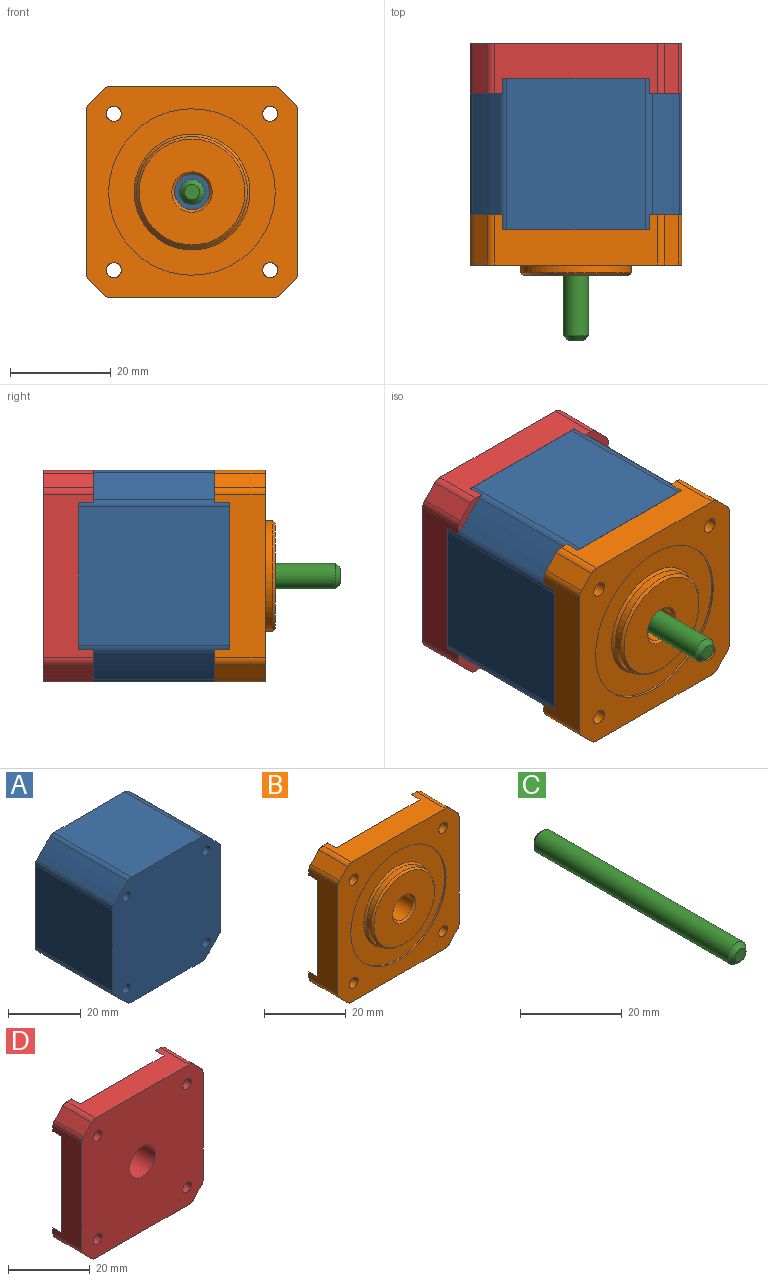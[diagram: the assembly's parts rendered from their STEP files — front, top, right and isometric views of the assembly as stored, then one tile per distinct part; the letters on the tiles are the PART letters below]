
ASSEMBLY  parts=4 mates=3
PART A: 22 faces, bbox 42x30x42 mm
  f0: cylinder r=55mm len=30mm, axis (0,1,0), area 230.4mm2, adj f8,f9,f10,f17
  f1: plane 30x27.54mm, normal (1,0,0), area 826.2mm2, adj f8,f9,f10,f11
  f2: cylinder r=55mm len=30mm, axis (0,1,0), area 230.4mm2, adj f8,f9,f11,f12
  f3: plane 30x27.54mm, normal (0,0,1), area 826.2mm2, adj f8,f9,f12,f13
  f4: cylinder r=55mm len=30mm, axis (0,1,0), area 230.4mm2, adj f8,f9,f13,f14
  f5: plane 30x27.54mm, normal (-1,0,0), area 826.2mm2, adj f8,f9,f14,f15
  f6: cylinder r=55mm len=30mm, axis (0,1,0), area 230.4mm2, adj f8,f9,f15,f16
  f7: plane 30x27.54mm, normal (0,0,-1), area 826.2mm2, adj f8,f9,f16,f17
  f8: plane 42x42mm, normal (0,-1,0), area 1655.7mm2, adj f0,f1,f2,f3,f4,f5,f6,f7
  f9: plane 42x42mm, normal (0,1,0), area 1655.7mm2, adj f0,f1,f2,f3,f4,f5,f6,f7
  f10: cylinder r=2mm len=30mm, axis (0,1,0), area 42.9mm2, adj f0,f1,f8,f9
  f11: cylinder r=2mm len=30mm, axis (0,1,0), area 42.9mm2, adj f1,f2,f8,f9
  f12: cylinder r=2mm len=30mm, axis (0,1,0), area 42.9mm2, adj f2,f3,f8,f9
  f13: cylinder r=2mm len=30mm, axis (0,1,0), area 42.9mm2, adj f3,f4,f8,f9
  f14: cylinder r=2mm len=30mm, axis (0,1,0), area 42.9mm2, adj f4,f5,f8,f9
  f15: cylinder r=2mm len=30mm, axis (0,1,0), area 42.9mm2, adj f5,f6,f8,f9
  f16: cylinder r=2mm len=30mm, axis (0,1,0), area 42.9mm2, adj f6,f7,f8,f9
  f17: cylinder r=2mm len=30mm, axis (0,1,0), area 42.9mm2, adj f0,f7,f8,f9
  f18: cylinder r=1.5mm len=30mm, axis (0,-1,0), area 282.7mm2, adj f8,f9
  f19: cylinder r=1.5mm len=30mm, axis (0,-1,0), area 282.7mm2, adj f8,f9
  f20: cylinder r=1.5mm len=30mm, axis (0,-1,0), area 282.7mm2, adj f8,f9
  f21: cylinder r=1.5mm len=30mm, axis (0,-1,0), area 282.7mm2, adj f8,f9
PART B: 38 faces, bbox 42x12x42 mm
  f0: plane 32.34x10mm, normal (1,0,0), area 236.4mm2, adj f3,f4,f9,f20,f21,f29,f31,f32
  f1: plane 32.34x10mm, normal (0,0,1), area 236.4mm2, adj f2,f3,f9,f18,f19,f29,f30,f31
  f2: plane 6.49x6.49mm, normal (0,1,0), area 11.7mm2, adj f1,f7,f13,f19,f23,f30
  f3: plane 6.49x6.49mm, normal (0,1,0), area 11.7mm2, adj f0,f1,f12,f18,f21,f31
  f4: plane 6.49x6.49mm, normal (0,1,0), area 11.7mm2, adj f0,f8,f11,f20,f25,f32
  f5: plane 6.49x6.49mm, normal (0,1,0), area 11.7mm2, adj f7,f8,f10,f22,f24,f33
  f6: cylinder r=3.5mm len=8.5mm, axis (0,-1,0), area 186.9mm2, adj f27,f29
  f7: plane 32.34x10mm, normal (-1,0,0), area 236.4mm2, adj f2,f5,f9,f22,f23,f29,f30,f33
  f8: plane 32.34x10mm, normal (0,0,-1), area 236.4mm2, adj f4,f5,f9,f24,f25,f29,f32,f33
  f9: plane 42x42mm, normal (0,-1,0), area 847.7mm2, adj f0,f1,f7,f8,f10,f11,f12,f13
  f10: plane 10x2.83mm, normal (-0.71,0,-0.71), area 40mm2, adj f5,f9,f22,f24
  f11: plane 10x2.83mm, normal (0.71,0,-0.71), area 40mm2, adj f4,f9,f20,f25
  f12: plane 10x2.83mm, normal (0.71,0,0.71), area 40mm2, adj f3,f9,f18,f21
  f13: plane 10x2.83mm, normal (-0.71,0,0.71), area 40mm2, adj f2,f9,f19,f23
  f14: cylinder r=16.5mm len=33mm, axis (0,-1,0), area 51.8mm2, adj f9,f15
  f15: plane 33x33mm, normal (0,-1,0), area 439.8mm2, adj f14,f26
  f16: cylinder r=11mm len=22mm, axis (0,1,0), area 103.7mm2, adj f26,f28
  f17: plane 21x21mm, normal (0,-1,0), area 296.1mm2, adj f27,f28
  f18: cylinder r=2mm len=10mm, axis (0,-1,0), area 15.7mm2, adj f1,f3,f9,f12
  f19: cylinder r=2mm len=10mm, axis (0,-1,0), area 15.7mm2, adj f1,f2,f9,f13
  f20: cylinder r=2mm len=10mm, axis (0,1,0), area 15.7mm2, adj f0,f4,f9,f11
  f21: cylinder r=2mm len=10mm, axis (0,1,0), area 15.7mm2, adj f0,f3,f9,f12
  f22: cylinder r=2mm len=10mm, axis (0,-1,0), area 15.7mm2, adj f5,f7,f9,f10
  f23: cylinder r=2mm len=10mm, axis (0,-1,0), area 15.7mm2, adj f2,f7,f9,f13
  f24: cylinder r=2mm len=10mm, axis (0,1,0), area 15.7mm2, adj f5,f8,f9,f10
  f25: cylinder r=2mm len=10mm, axis (0,1,0), area 15.7mm2, adj f4,f8,f9,f11
  f26: cone r=11mm half-angle=45deg, axis (0,1,0), area 50mm2, adj f15,f16
  f27: cone r=3.5mm half-angle=45deg, axis (0,-1,0), area 16.7mm2, adj f6,f17
  f28: cone r=10.5mm half-angle=45deg, axis (0,1,0), area 47.8mm2, adj f16,f17
  f29: plane 42x42mm, normal (0,1,0), area 1617.7mm2, adj f0,f1,f6,f7,f8,f30,f31,f32
  f30: cylinder r=55mm len=6.49mm, axis (0,1,0), area 27.6mm2, adj f1,f2,f7,f29
  f31: cylinder r=55mm len=6.49mm, axis (0,1,0), area 27.6mm2, adj f0,f1,f3,f29
  f32: cylinder r=55mm len=6.49mm, axis (0,1,0), area 27.6mm2, adj f0,f4,f8,f29
  f33: cylinder r=55mm len=6.49mm, axis (0,1,0), area 27.6mm2, adj f5,f7,f8,f29
  f34: cylinder r=1.5mm len=7mm, axis (0,-1,0), area 66mm2, adj f9,f29
  f35: cylinder r=1.5mm len=7mm, axis (0,-1,0), area 66mm2, adj f9,f29
  f36: cylinder r=1.5mm len=7mm, axis (0,-1,0), area 66mm2, adj f9,f29
  f37: cylinder r=1.5mm len=7mm, axis (0,-1,0), area 66mm2, adj f9,f29
PART C: 5 faces, bbox 5x56x5 mm
  f0: cylinder r=2.5mm len=54mm, axis (0,1,0), area 848.2mm2, adj f3,f4
  f1: plane 3x3mm, normal (0,-1,0), area 7.1mm2, adj f4
  f2: plane 3x3mm, normal (0,1,0), area 7.1mm2, adj f3
  f3: cone r=2.5mm half-angle=45deg, axis (0,-1,0), area 17.8mm2, adj f0,f2
  f4: cone r=1.5mm half-angle=45deg, axis (0,1,0), area 17.8mm2, adj f0,f1
PART D: 31 faces, bbox 42x10x42 mm
  f0: plane 32.34x10mm, normal (1,0,0), area 236.4mm2, adj f3,f4,f8,f15,f16,f22,f23,f25
  f1: plane 32.34x10mm, normal (0,0,1), area 236.4mm2, adj f2,f3,f8,f13,f14,f21,f22,f25
  f2: plane 6.49x6.49mm, normal (0,1,0), area 11.7mm2, adj f1,f6,f12,f14,f18,f21
  f3: plane 6.49x6.49mm, normal (0,1,0), area 11.7mm2, adj f0,f1,f11,f13,f16,f22
  f4: plane 6.49x6.49mm, normal (0,1,0), area 11.7mm2, adj f0,f7,f10,f15,f20,f23
  f5: plane 6.49x6.49mm, normal (0,1,0), area 11.7mm2, adj f6,f7,f9,f17,f19,f24
  f6: plane 32.34x10mm, normal (-1,0,0), area 236.4mm2, adj f2,f5,f8,f17,f18,f21,f24,f25
  f7: plane 32.34x10mm, normal (0,0,-1), area 236.4mm2, adj f4,f5,f8,f19,f20,f23,f24,f25
  f8: plane 42x42mm, normal (0,-1,0), area 1639.4mm2, adj f0,f1,f6,f7,f9,f10,f11,f12
  f9: plane 10x2.83mm, normal (-0.71,0,-0.71), area 40mm2, adj f5,f8,f17,f19
  f10: plane 10x2.83mm, normal (0.71,0,-0.71), area 40mm2, adj f4,f8,f15,f20
  f11: plane 10x2.83mm, normal (0.71,0,0.71), area 40mm2, adj f3,f8,f13,f16
  f12: plane 10x2.83mm, normal (-0.71,0,0.71), area 40mm2, adj f2,f8,f14,f18
  f13: cylinder r=2mm len=10mm, axis (0,-1,0), area 15.7mm2, adj f1,f3,f8,f11
  f14: cylinder r=2mm len=10mm, axis (0,-1,0), area 15.7mm2, adj f1,f2,f8,f12
  f15: cylinder r=2mm len=10mm, axis (0,1,0), area 15.7mm2, adj f0,f4,f8,f10
  f16: cylinder r=2mm len=10mm, axis (0,1,0), area 15.7mm2, adj f0,f3,f8,f11
  f17: cylinder r=2mm len=10mm, axis (0,-1,0), area 15.7mm2, adj f5,f6,f8,f9
  f18: cylinder r=2mm len=10mm, axis (0,-1,0), area 15.7mm2, adj f2,f6,f8,f12
  f19: cylinder r=2mm len=10mm, axis (0,1,0), area 15.7mm2, adj f5,f7,f8,f9
  f20: cylinder r=2mm len=10mm, axis (0,1,0), area 15.7mm2, adj f4,f7,f8,f10
  f21: cylinder r=55mm len=6.49mm, axis (0,1,0), area 27.6mm2, adj f1,f2,f6,f25
  f22: cylinder r=55mm len=6.49mm, axis (0,1,0), area 27.6mm2, adj f0,f1,f3,f25
  f23: cylinder r=55mm len=6.49mm, axis (0,1,0), area 27.6mm2, adj f0,f4,f7,f25
  f24: cylinder r=55mm len=6.49mm, axis (0,1,0), area 27.6mm2, adj f5,f6,f7,f25
  f25: plane 42x42mm, normal (0,1,0), area 1592.6mm2, adj f0,f1,f6,f7,f21,f22,f23,f24
  f26: cylinder r=1.5mm len=7mm, axis (0,-1,0), area 66mm2, adj f8,f25
  f27: cylinder r=1.5mm len=7mm, axis (0,-1,0), area 66mm2, adj f8,f25
  f28: cylinder r=1.5mm len=7mm, axis (0,-1,0), area 66mm2, adj f8,f25
  f29: cylinder r=1.5mm len=7mm, axis (0,-1,0), area 66mm2, adj f8,f25
  f30: cylinder r=4.5mm len=9mm, axis (0,-1,0), area 197.9mm2, adj f8,f25
PLACE A t=(1.6,19.94,1.53)mm
PLACE B t=(1.6,7.94,1.53)mm fixed
PLACE C t=(1.6,25.44,1.53)mm
PLACE D rot(axis=(0,0,1),180deg) t=(1.6,31.94,1.53)mm
MATE fastened A.f19 <-> B.f34  axis (0,-1,0) through (-13.9,4.94,17.03)mm
MATE revolute C.f0 <-> B.f6  axis (0,-1,0) through (1.6,-17.06,1.53)mm
MATE fastened D.f29 <-> A.f19  axis (0,-1,0) through (-13.9,34.94,17.03)mm
